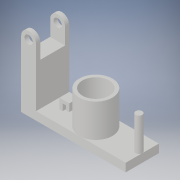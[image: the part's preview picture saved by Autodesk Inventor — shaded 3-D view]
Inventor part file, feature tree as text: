
AUTODESK INVENTOR PART (.ipt)
format: ipt  version: 2019 (Build 230136000, 136)  size: 180,224 bytes
history: native  units: in
note: dims shown in document units (in); Inventor stores cm internally (conversion verified against a paired STEP export)
features: extrude x6, sketch x5
ambient origin geometry x8: Origin, YZ Plane, XZ Plane, XY Plane, X Axis, Y Axis, Z Axis, Center Point
bodies: Solid1 (feature_tree)
feature tree (11):
  extrude  "Extrusion1"  Depth=0.1969in
  sketch  "Sketch2"  dims[d6=0.1772in d7=0.1969in]
  extrude  "Extrusion5"  Depth=0.1969in
  extrude  "Extrusion6"  Depth=2.126in
  extrude  "Extrusion7"  Depth=0.7874in
  extrude  "Extrusion8"  Depth=0.7874in
  extrude  "Extrusion9"  Depth=0.1575in
  sketch  "Sketch1"  dims[d0=1.5748in d2=0.1969in]
  sketch  "Sketch7"  dims[d8=0.3543in d9=2.126in]
  sketch  "Sketch9"  dims[d10=0.7874in d11=0.0in d12=0.1181in]
  sketch  "Sketch10"  dims[d13=0.2559in d14=0.7874in d16=1.0236in d19=0.3937in d20=0.1575in d21=0.3937in d22=0.5512in d40=0.5512in d41=0.5512in d42=0.5906in d43=0.5512in d44=0.0in d47=1.2795in d48=0.7874in d49=0.0in d50=0.6299in d51=0.9843in d52=0.0in d53=0.2362in d54=0.1575in d55=0.315in d56=0.2362in d57=0.2362in d58=0.0in d59=0.0787in d60=0.0787in d61=0.1575in d62=0.0591in d63=0.1575in d64=0.0in]
